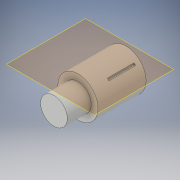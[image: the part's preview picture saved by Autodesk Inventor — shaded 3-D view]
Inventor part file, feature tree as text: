
AUTODESK INVENTOR PART (.ipt)
format: ipt  version: 2019 (Build 230136000, 136)  size: 134,656 bytes
history: native  units: mm
features: extrude x3, sketch x3, fillet x2, plane x1
ambient origin geometry x8: Origin, YZ Plane, XZ Plane, XY Plane, X Axis, Y Axis, Z Axis, Center Point
bodies: Body1 (feature_tree)
feature tree (9):
  extrude  "擠出2"  Depth=15.0mm
  extrude  "擠出3"  Depth=18.0mm TaperAngle=0.0deg
  plane  "工作平面2"
  extrude  "擠出5"  Depth=10.0mm
  fillet  "圓角1"  Radius=9.0mm
  fillet  "圓角2"  Radius=5.0mm
  sketch  "草圖2"
  sketch  "草圖3"
  sketch  "草圖5"
